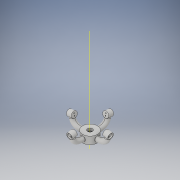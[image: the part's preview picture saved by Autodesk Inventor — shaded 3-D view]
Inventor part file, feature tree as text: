
AUTODESK INVENTOR PART (.ipt)
format: ipt  version: 2018 (Build 220112000, 112)  size: 412,160 bytes
history: native  units: in
note: dims shown in document units (in); Inventor stores cm internally (conversion verified against a paired STEP export)
features: sketch x8, extrude x8, other x4, plane x1, sweep x1, pattern_circular x1, projected_geometry x1
ambient origin geometry x8: Origin, YZ Plane, XZ Plane, XY Plane, X Axis, Y Axis, Z Axis, Center Point
bodies: Body1 (feature_tree)
feature tree (24):
  other  "led_stand.ipt"
  sketch  "Sketch4"  dims[d2=0.3937in d3=0.125in]
  extrude  "Extrusion1"  Depth=0.125in
  extrude  "Extrusion2"  Depth=0.125in TaperAngle=0.0deg
  extrude  "Extrusion3"  Depth=0.125in
  extrude  "Extrusion4"  Depth=0.75in
  sketch  "Sketch8"  dims[d12=0.5in d13=0.0in d14=0.0687in]
  extrude  "Extrusion5"  Depth=0.0687in
  extrude  "Extrusion6"  Depth=0.0394in
  extrude  "Extrusion7"  Depth=0.2362in
  sketch  "Sketch9"  dims[d15=1.0in d16=0.0in d17=0.0394in]
  plane  "Work Plane1"
  sweep  "Sweep1"
  extrude  "Extrusion8"  Depth=1.0in TaperAngle=0.0deg
  pattern_circular  "Circular Pattern1"  [2 undecoded]
  sketch  "Sketch5"  dims[d4=0.125in d5=0.25in d6=0.0in]
  sketch  "Sketch6"  dims[d7=0.125in d8=0.0in d9=0.5in]
  sketch  "Sketch7"  dims[d10=0.5in d11=0.75in]
  projected_geometry  "Projected Loop1"
  sketch  "Sketch10"  dims[d18=0.0689in d19=0.2362in]
  other  "Work Axis2"
  other  "Work Axis3"
  other  "Work Axis4"
  sketch  "Sketch11"  dims[d20=0.0312in d21=0.1476in d22=1.0in d23=0.0in d24=0.25in d25=0.0in d26=0.1875in d27=0.0in d29=0.0625in d30=0.25in d31=0.0in d32=0.0in d33=1.5748in d34=360.0deg d36=0.0938in d37=0.0in]
note: 2 required parameter values undecoded (feature->parameter linkage not recoverable at this tier; creation-order binding heuristic only, values carry confidence <= 0.55)
